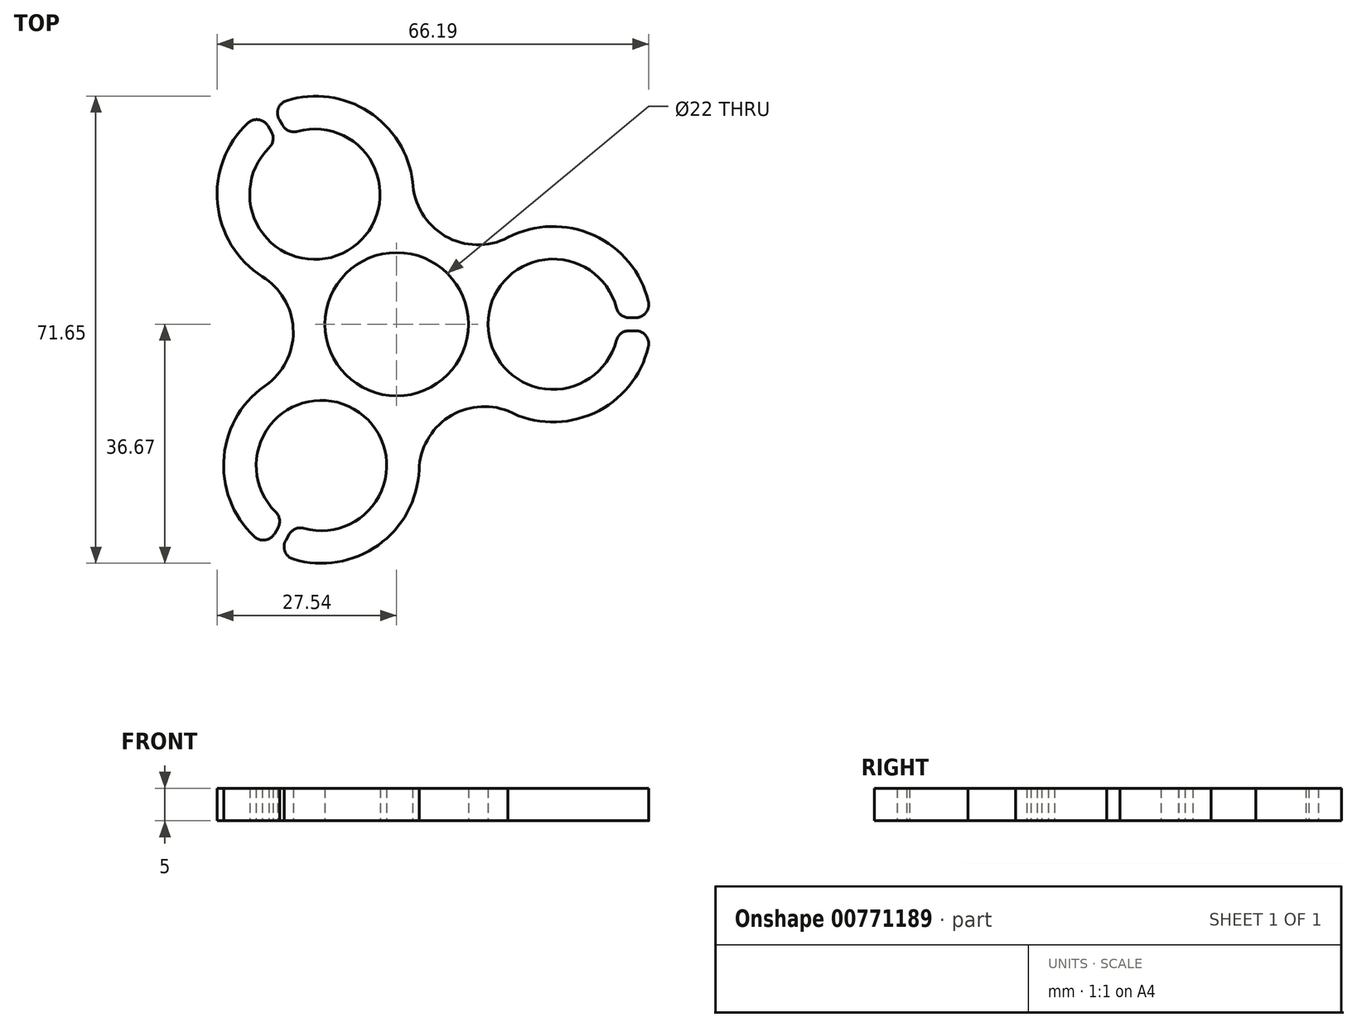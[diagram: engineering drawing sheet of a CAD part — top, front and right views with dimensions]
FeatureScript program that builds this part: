
annotation { "Feature Type Name" : "Feature", "Feature Type Description" : "" }
export const myFeature = defineFeature(function(context is Context, id is Id, definition is map)
    precondition{}
    {
        {
            var Q0;
            Q0=qCreatedBy(makeId("Top.planeOp"),FACE);
            var sketch = newSketch(context, id + "F0", { "sketchPlane" : qUnion([Q0])});
            skCircle(sketch, "E0", {"center": v(0, 0) * mm, "radius": 11 * mm});
            skArc(sketch, "E1", {"start": v(33.68, 2.5) * mm, "mid": v(14, 0) * mm, "end": v(33.68, -2.5) * mm});
            skArc(sketch, "E2.0", {"start": v(38.6, 3.46) * mm, "mid": v(30.24, 13.64) * mm, "end": v(17.08, 13.3) * mm});
            skLineSegment(sketch, "E3", {"start": v(35.62, 1) * mm, "end": v(36.65, 1) * mm});
            skLineSegment(sketch, "E4", {"start": v(35.62, -1) * mm, "end": v(36.65, -1) * mm});
            skArc(sketch, "E5.trimOffspring", {"start": v(17.08, -13.3) * mm, "mid": v(30.24, -13.64) * mm, "end": v(38.6, -3.46) * mm});
            skPoint(sketch, "E6.visualSharp", {"position": v(12.75, 9.92) * mm});
            skArc(sketch, "E6.filletArc", {"start": v(2.47, 21.81) * mm, "mid": v(7.43, 13.54) * mm, "end": v(17.08, 13.3) * mm});
            skPoint(sketch, "E7.visualSharp", {"position": v(12.75, -9.92) * mm});
            skArc(sketch, "E8.1.0", {"start": v(-22.83, 30.85) * mm, "mid": v(-27.47, 18.53) * mm, "end": v(-20.6, 7.3) * mm});
            skArc(sketch, "E8.1.1", {"start": v(-19.54, 27.08) * mm, "mid": v(-7.54, 11.28) * mm, "end": v(-15.21, 29.58) * mm});
            skArc(sketch, "E8.1.2", {"start": v(2.47, 21.81) * mm, "mid": v(-4.27, 32.57) * mm, "end": v(-16.86, 34.3) * mm});
            skLineSegment(sketch, "E8.1.3", {"start": v(-17.48, 30.5) * mm, "end": v(-18, 31.4) * mm});
            skLineSegment(sketch, "E8.1.4", {"start": v(-19.21, 29.5) * mm, "end": v(-19.73, 30.4) * mm});
            skArc(sketch, "E8.1.6", {"start": v(-19.6, -9.02) * mm, "mid": v(-15.87, -0.6) * mm, "end": v(-20.6, 7.3) * mm});
            skArc(sketch, "E8.2.0", {"start": v(-15.84, -36.04) * mm, "mid": v(-2.85, -33.9) * mm, "end": v(3.45, -22.33) * mm});
            skArc(sketch, "E8.2.1", {"start": v(-14.21, -31.3) * mm, "mid": v(-6.54, -13.01) * mm, "end": v(-18.54, -28.8) * mm});
            skArc(sketch, "E8.2.2", {"start": v(-19.6, -9.02) * mm, "mid": v(-26.47, -20.26) * mm, "end": v(-21.83, -32.58) * mm});
            skLineSegment(sketch, "E8.2.3", {"start": v(-18.21, -31.23) * mm, "end": v(-18.73, -32.13) * mm});
            skLineSegment(sketch, "E8.2.4", {"start": v(-16.48, -32.23) * mm, "end": v(-17, -33.13) * mm});
            skArc(sketch, "E8.2.6", {"start": v(17.08, -13.3) * mm, "mid": v(7.92, -14.28) * mm, "end": v(3.45, -22.33) * mm});
            skPoint(sketch, "E8.center", {"position": v(-0.03, -0.58) * mm});
            skPoint(sketch, "E9.orphan", {"position": v(-14.99, -1.03) * mm});
            skPoint(sketch, "E10.orphan", {"position": v(-15.86, -0.78) * mm});
            skPoint(sketch, "E11.orphan", {"position": v(7.06, 12.6) * mm});
            skPoint(sketch, "E12.orphan", {"position": v(7.85, 13.3) * mm});
            skPoint(sketch, "E13.orphan", {"position": v(8.07, -14.2) * mm});
            skPoint(sketch, "E14.orphan", {"position": v(7.85, -13.3) * mm});
            skPoint(sketch, "E15.visualSharp", {"position": v(38.97, 1) * mm});
            skArc(sketch, "E15.filletArc", {"start": v(36.65, 1) * mm, "mid": v(38.22, 1.76) * mm, "end": v(38.6, 3.46) * mm});
            skPoint(sketch, "E16.visualSharp", {"position": v(38.97, -1) * mm});
            skArc(sketch, "E16.filletArc", {"start": v(38.6, -3.46) * mm, "mid": v(38.22, -1.76) * mm, "end": v(36.65, -1) * mm});
            skPoint(sketch, "E17.visualSharp", {"position": v(-19.14, 33.39) * mm});
            skArc(sketch, "E17.filletArc", {"start": v(-16.86, 34.3) * mm, "mid": v(-18.13, 33.13) * mm, "end": v(-18, 31.4) * mm});
            skPoint(sketch, "E18.visualSharp", {"position": v(-20.89, 32.4) * mm});
            skArc(sketch, "E18.filletArc", {"start": v(-19.73, 30.4) * mm, "mid": v(-21.17, 31.37) * mm, "end": v(-22.83, 30.85) * mm});
            skPoint(sketch, "E19.visualSharp", {"position": v(-19.89, -34.13) * mm});
            skArc(sketch, "E19.filletArc", {"start": v(-21.83, -32.58) * mm, "mid": v(-20.17, -33.1) * mm, "end": v(-18.73, -32.13) * mm});
            skPoint(sketch, "E20.visualSharp", {"position": v(-18.16, -35.13) * mm});
            skArc(sketch, "E20.filletArc", {"start": v(-17, -33.13) * mm, "mid": v(-17.12, -34.86) * mm, "end": v(-15.84, -36.04) * mm});
            skPoint(sketch, "E21.visualSharp", {"position": v(-15.65, -30.79) * mm});
            skArc(sketch, "E21.filletArc", {"start": v(-14.21, -31.3) * mm, "mid": v(-15.5, -31.38) * mm, "end": v(-16.48, -32.23) * mm});
            skPoint(sketch, "E22.visualSharp", {"position": v(-17.38, -29.79) * mm});
            skArc(sketch, "E22.filletArc", {"start": v(-18.21, -31.23) * mm, "mid": v(-17.96, -29.96) * mm, "end": v(-18.54, -28.8) * mm});
            skPoint(sketch, "E23.visualSharp", {"position": v(33.95, -1) * mm});
            skArc(sketch, "E23.filletArc", {"start": v(35.62, -1) * mm, "mid": v(34.4, -1.42) * mm, "end": v(33.68, -2.5) * mm});
            skPoint(sketch, "E24.visualSharp", {"position": v(33.95, 1) * mm});
            skArc(sketch, "E24.filletArc", {"start": v(33.68, 2.5) * mm, "mid": v(34.4, 1.42) * mm, "end": v(35.62, 1) * mm});
            skPoint(sketch, "E25.visualSharp", {"position": v(-16.65, 29.06) * mm});
            skArc(sketch, "E25.filletArc", {"start": v(-17.48, 30.5) * mm, "mid": v(-16.5, 29.65) * mm, "end": v(-15.21, 29.58) * mm});
            skPoint(sketch, "E26.visualSharp", {"position": v(-18.38, 28.06) * mm});
            skArc(sketch, "E26.filletArc", {"start": v(-19.54, 27.08) * mm, "mid": v(-18.96, 28.23) * mm, "end": v(-19.21, 29.5) * mm});
            skSolve(sketch);
        }
        {
            var Q0;
            Q0=makeQuery(id+"F0.imprint","IMPRINT",FACE,{"disambiguationData":[TD([[makeQuery(id+"F0.imprint","IMPRINT",EDGE,{"derivedFrom":sQuery(id+"F0.wireOp",EDGE,"E0")}),-1.0]])]});
            extrude(context, id + "F1", {"entities" : qUnion([Q0]), "depth" : 5 * mm, "offsetDistance" : 25 * mm});
        }
    });
